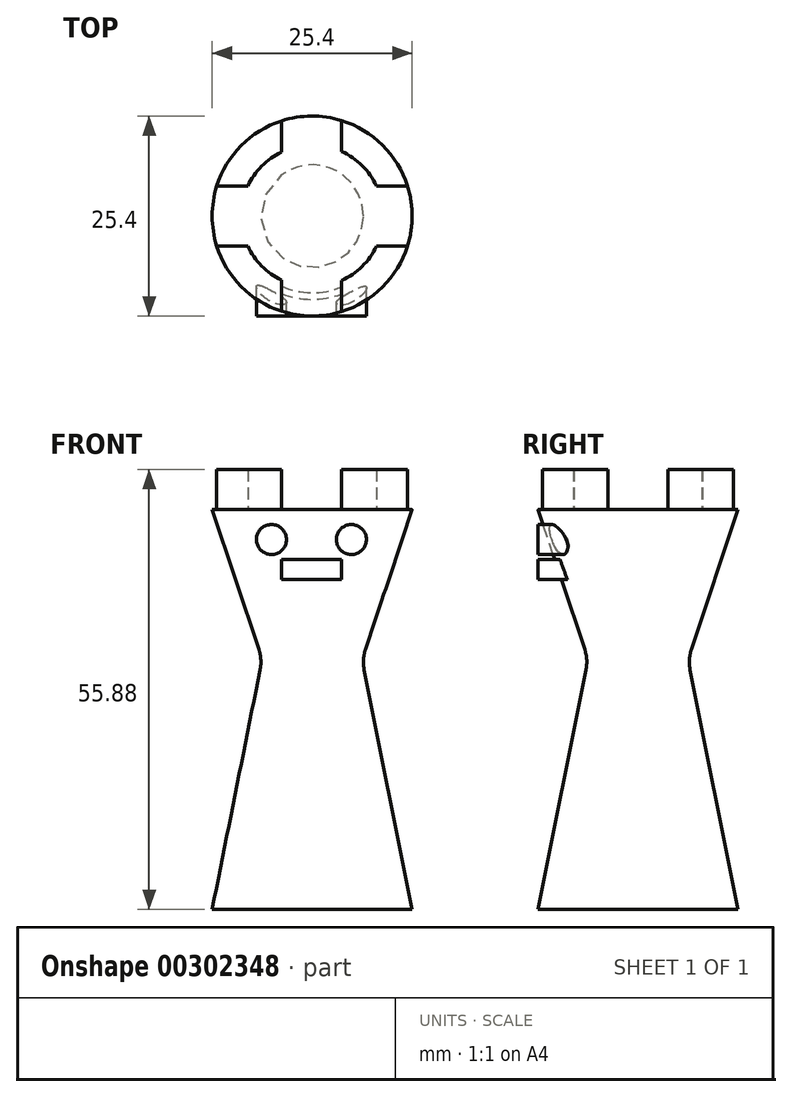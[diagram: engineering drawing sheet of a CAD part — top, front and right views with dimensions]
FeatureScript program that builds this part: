
annotation { "Feature Type Name" : "Feature", "Feature Type Description" : "" }
export const myFeature = defineFeature(function(context is Context, id is Id, definition is map)
    precondition{}
    {
        {
            var Q0;
            Q0=qCreatedBy(makeId("Front.planeOp"),FACE);
            var sketch = newSketch(context, id + "F0", { "sketchPlane" : qUnion([Q0])});
            skLineSegment(sketch, "E0", {"start": v(0, 0) * mm, "end": v(25.4, 0) * mm});
            skLineSegment(sketch, "E1", {"start": v(25.4, 0) * mm, "end": v(19.05, 31.75) * mm});
            skLineSegment(sketch, "E2", {"start": v(19.05, 31.75) * mm, "end": v(25.4, 50.8) * mm});
            skLineSegment(sketch, "E3", {"start": v(25.4, 50.8) * mm, "end": v(0, 50.8) * mm});
            skLineSegment(sketch, "E4", {"start": v(0, 50.8) * mm, "end": v(6.35, 31.75) * mm});
            skLineSegment(sketch, "E5", {"start": v(6.35, 31.75) * mm, "end": v(0, 0) * mm});
            skLineSegment(sketch, "E6", {"start": v(12.7, 50.8) * mm, "end": v(12.7, 0) * mm});
            skLineSegment(sketch, "E7", {"start": v(19.05, 31.75) * mm, "end": v(6.35, 31.75) * mm, "construction": true});
            skPoint(sketch, "E8", {"position": v(12.7, 31.75) * mm});
            skSolve(sketch);
        }
        {
            var Q0;
            {var subQ3=sQuery(id+"F0.wireOp",EDGE,"E1");Q0=makeQuery(id+"F0.imprint","IMPRINT",FACE,{"disambiguationData":[TD([[makeQuery(id+"F0.imprint","IMPRINT",EDGE,{"derivedFrom":subQ3}),1.0]])]});}
            var Q1;
            Q1=sQuery(id+"F0.wireOp",EDGE,"E6");
            revolve(context, id + "F1", {"entities" : qUnion([Q0]), "axis" : qUnion([Q1]), "revolveType" : RevolveType.FULL});
        }
        {
            var Q0;
            Q0=makeQuery(id+"F1.opRevolve","SWEPT_FACE",FACE,{"disambiguationData":[OSD([sQuery(id+"F0.wireOp",EDGE,"E3")])]});
            var sketch = newSketch(context, id + "F2", { "sketchPlane" : qUnion([Q0])});
            skLineSegment(sketch, "E9.bottom", {"start": v(12.7, 12.7) * mm, "end": v(12.7, 12.7) * mm});
            skLineSegment(sketch, "E9.top", {"start": v(12.7, -12.7) * mm, "end": v(12.7, -12.7) * mm});
            skLineSegment(sketch, "E9.left", {"start": v(0, 0) * mm, "end": v(0, 0) * mm});
            skLineSegment(sketch, "E9.right", {"start": v(25.4, 0) * mm, "end": v(25.4, 0) * mm});
            skLineSegment(sketch, "E10", {"start": v(12.7, -12.7) * mm, "end": v(12.7, 0) * mm});
            skLineSegment(sketch, "E11", {"start": v(12.7, 0) * mm, "end": v(12.7, 12.7) * mm});
            skLineSegment(sketch, "E12", {"start": v(0, 12.7) * mm, "end": v(25.4, -12.7) * mm, "construction": true});
            skPoint(sketch, "E13.visualSharp", {"position": v(0, 12.7) * mm});
            skArc(sketch, "E13.filletArc", {"start": v(12.7, 12.7) * mm, "mid": v(3.72, 8.98) * mm, "end": v(0, 0) * mm});
            skPoint(sketch, "E14.visualSharp", {"position": v(25.4, 12.7) * mm});
            skArc(sketch, "E14.filletArc", {"start": v(25.4, 0) * mm, "mid": v(21.68, 8.98) * mm, "end": v(12.7, 12.7) * mm});
            skPoint(sketch, "E15.visualSharp", {"position": v(25.4, -12.7) * mm});
            skArc(sketch, "E15.filletArc", {"start": v(12.7, -12.7) * mm, "mid": v(21.68, -8.98) * mm, "end": v(25.4, 0) * mm});
            skPoint(sketch, "E16.visualSharp", {"position": v(0, -12.7) * mm});
            skArc(sketch, "E16.filletArc", {"start": v(0, 0) * mm, "mid": v(3.72, -8.98) * mm, "end": v(12.7, -12.7) * mm});
            skLineSegment(sketch, "E17.bottom", {"start": v(12.6, 8.98) * mm, "end": v(12.8, 8.98) * mm});
            skLineSegment(sketch, "E17.top", {"start": v(12.6, -8.98) * mm, "end": v(12.8, -8.98) * mm});
            skLineSegment(sketch, "E17.left", {"start": v(3.72, 0.1) * mm, "end": v(3.72, -0.1) * mm});
            skLineSegment(sketch, "E17.right", {"start": v(21.68, 0.1) * mm, "end": v(21.68, -0.1) * mm});
            skPoint(sketch, "E18.visualSharp", {"position": v(3.72, 8.98) * mm});
            skArc(sketch, "E18.filletArc", {"start": v(12.6, 8.98) * mm, "mid": v(6.32, 6.38) * mm, "end": v(3.72, 0.1) * mm});
            skPoint(sketch, "E19.visualSharp", {"position": v(21.68, 8.98) * mm});
            skArc(sketch, "E19.filletArc", {"start": v(21.68, 0.1) * mm, "mid": v(19.08, 6.38) * mm, "end": v(12.8, 8.98) * mm});
            skPoint(sketch, "E20.visualSharp", {"position": v(21.68, -8.98) * mm});
            skArc(sketch, "E20.filletArc", {"start": v(12.8, -8.98) * mm, "mid": v(19.08, -6.38) * mm, "end": v(21.68, -0.1) * mm});
            skPoint(sketch, "E21.visualSharp", {"position": v(3.72, -8.98) * mm});
            skArc(sketch, "E21.filletArc", {"start": v(3.72, -0.1) * mm, "mid": v(6.32, -6.38) * mm, "end": v(12.6, -8.98) * mm});
            skSolve(sketch);
        }
        {
            var Q0;
            {var subQ1=sQuery(id+"F2.wireOp",EDGE,"E13.filletArc");Q0=makeQuery(id+"F2.imprint","IMPRINT",FACE,{"disambiguationData":[TD([[makeQuery(id+"F2.imprint","IMPRINT",EDGE,{"derivedFrom":subQ1}),1.0]])]});}
            var Q1;
            {var subQ1=sQuery(id+"F2.wireOp",EDGE,"E14.filletArc");Q1=makeQuery(id+"F2.imprint","IMPRINT",FACE,{"disambiguationData":[TD([[makeQuery(id+"F2.imprint","IMPRINT",EDGE,{"derivedFrom":subQ1}),1.0]])]});}
            extrude(context, id + "F3", {"entities" : qUnion([Q0, Q1]), "operationType" : NewBodyOperationType.ADD, "depth" : 5.08 * mm});
        }
        {
            var Q0;
            Q0=qCreatedBy(makeId("Front.planeOp"),FACE);
            cPlane(context, id + "F4", {"entities" : qUnion([Q0]), "cplaneType" : CPlaneType.OFFSET, "offset" : 25.4 * mm, "width" : 152.4 * mm, "height" : 152.4 * mm});
        }
        {
            var Q0;
            Q0=qCreatedBy(id+"F4.planeOp",FACE);
            var sketch = newSketch(context, id + "F5", { "sketchPlane" : qUnion([Q0])});
            skLineSegment(sketch, "E22.bottom", {"start": v(8.8, 55.88) * mm, "end": v(16.42, 55.88) * mm});
            skLineSegment(sketch, "E22.top", {"start": v(8.8, 50.8) * mm, "end": v(16.42, 50.8) * mm});
            skLineSegment(sketch, "E22.left", {"start": v(8.8, 55.88) * mm, "end": v(8.8, 50.8) * mm});
            skLineSegment(sketch, "E22.right", {"start": v(16.42, 55.88) * mm, "end": v(16.42, 50.8) * mm});
            skSolve(sketch);
        }
        {
            var Q0;
            Q0=makeQuery(id+"F5.imprint","IMPRINT",FACE,{"disambiguationData":[TD([[makeQuery(id+"F5.imprint","IMPRINT",EDGE,{"derivedFrom":sQuery(id+"F5.wireOp",EDGE,"E22.bottom")}),-1.0]])]});
            extrude(context, id + "F6", {"entities" : qUnion([Q0]), "operationType" : NewBodyOperationType.REMOVE, "endBound" : BoundingType.THROUGH_ALL, "oppositeDirection" : true, "depth" : 25.4 * mm});
        }
        {
            var Q0;
            Q0=qCreatedBy(makeId("Right.planeOp"),FACE);
            cPlane(context, id + "F7", {"entities" : qUnion([Q0]), "cplaneType" : CPlaneType.OFFSET, "offset" : 25.4 * mm, "width" : 152.4 * mm, "height" : 152.4 * mm});
        }
        {
            var Q0;
            Q0=qCreatedBy(id+"F7.planeOp",FACE);
            var sketch = newSketch(context, id + "F8", { "sketchPlane" : qUnion([Q0])});
            skLineSegment(sketch, "E23.bottom", {"start": v(-3.81, 55.88) * mm, "end": v(3.81, 55.88) * mm});
            skLineSegment(sketch, "E23.top", {"start": v(-3.8, 50.8) * mm, "end": v(3.81, 50.8) * mm});
            skLineSegment(sketch, "E23.left", {"start": v(-3.8, 55.88) * mm, "end": v(-3.8, 50.8) * mm});
            skLineSegment(sketch, "E23.right", {"start": v(3.81, 55.88) * mm, "end": v(3.81, 50.8) * mm});
            skSolve(sketch);
        }
        {
            var Q0;
            Q0=makeQuery(id+"F8.imprint","IMPRINT",FACE,{"disambiguationData":[TD([[makeQuery(id+"F8.imprint","IMPRINT",EDGE,{"derivedFrom":sQuery(id+"F8.wireOp",EDGE,"E23.bottom")}),-1.0]])]});
            extrude(context, id + "F9", {"entities" : qUnion([Q0]), "operationType" : NewBodyOperationType.REMOVE, "endBound" : BoundingType.THROUGH_ALL, "oppositeDirection" : true, "depth" : 25.4 * mm});
        }
        {
            var Q0;
            Q0=qCreatedBy(makeId("Front.planeOp"),FACE);
            var sketch = newSketch(context, id + "F10", { "sketchPlane" : qUnion([Q0])});
            skCircle(sketch, "E24", {"center": v(7.53, 46.99) * mm, "radius": 1.9 * mm});
            skCircle(sketch, "E25", {"center": v(17.69, 46.99) * mm, "radius": 1.9 * mm});
            skLineSegment(sketch, "E26.bottom", {"start": v(8.8, 44.45) * mm, "end": v(16.42, 44.45) * mm});
            skLineSegment(sketch, "E26.top", {"start": v(8.8, 41.9) * mm, "end": v(16.42, 41.9) * mm});
            skLineSegment(sketch, "E26.left", {"start": v(8.8, 44.45) * mm, "end": v(8.8, 41.9) * mm});
            skLineSegment(sketch, "E26.right", {"start": v(16.42, 44.45) * mm, "end": v(16.42, 41.9) * mm});
            skLineSegment(sketch, "E27", {"start": v(12.6, 50.8) * mm, "end": v(12.6, 46.99) * mm, "construction": true});
            skLineSegment(sketch, "E28", {"start": v(17.69, 46.99) * mm, "end": v(7.53, 46.99) * mm, "construction": true});
            skLineSegment(sketch, "E29", {"start": v(12.6, 46.99) * mm, "end": v(12.6, 44.45) * mm, "construction": true});
            skSolve(sketch);
        }
        {
            var Q0;
            Q0 = qSketchRegion(id + "F10", true);
            extrude(context, id + "F11", {"entities" : qUnion([Q0]), "operationType" : NewBodyOperationType.ADD, "depth" : 12.7 * mm});
        }
        {
            var Q0;
            Q0=makeQuery(id+"F1.opRevolve","SWEPT_EDGE",EDGE,{"disambiguationData":[OSD([sQuery(id+"F0.wireOp",EDGE,"E1"),sQuery(id+"F0.wireOp",EDGE,"E2")])]});
            fillet(context, id + "F12", {"entities" : qUnion([Q0]), "radius" : 5.08 * mm, "tangentPropagation" : true, "allowEdgeOverflow" : false});
        }
    });
